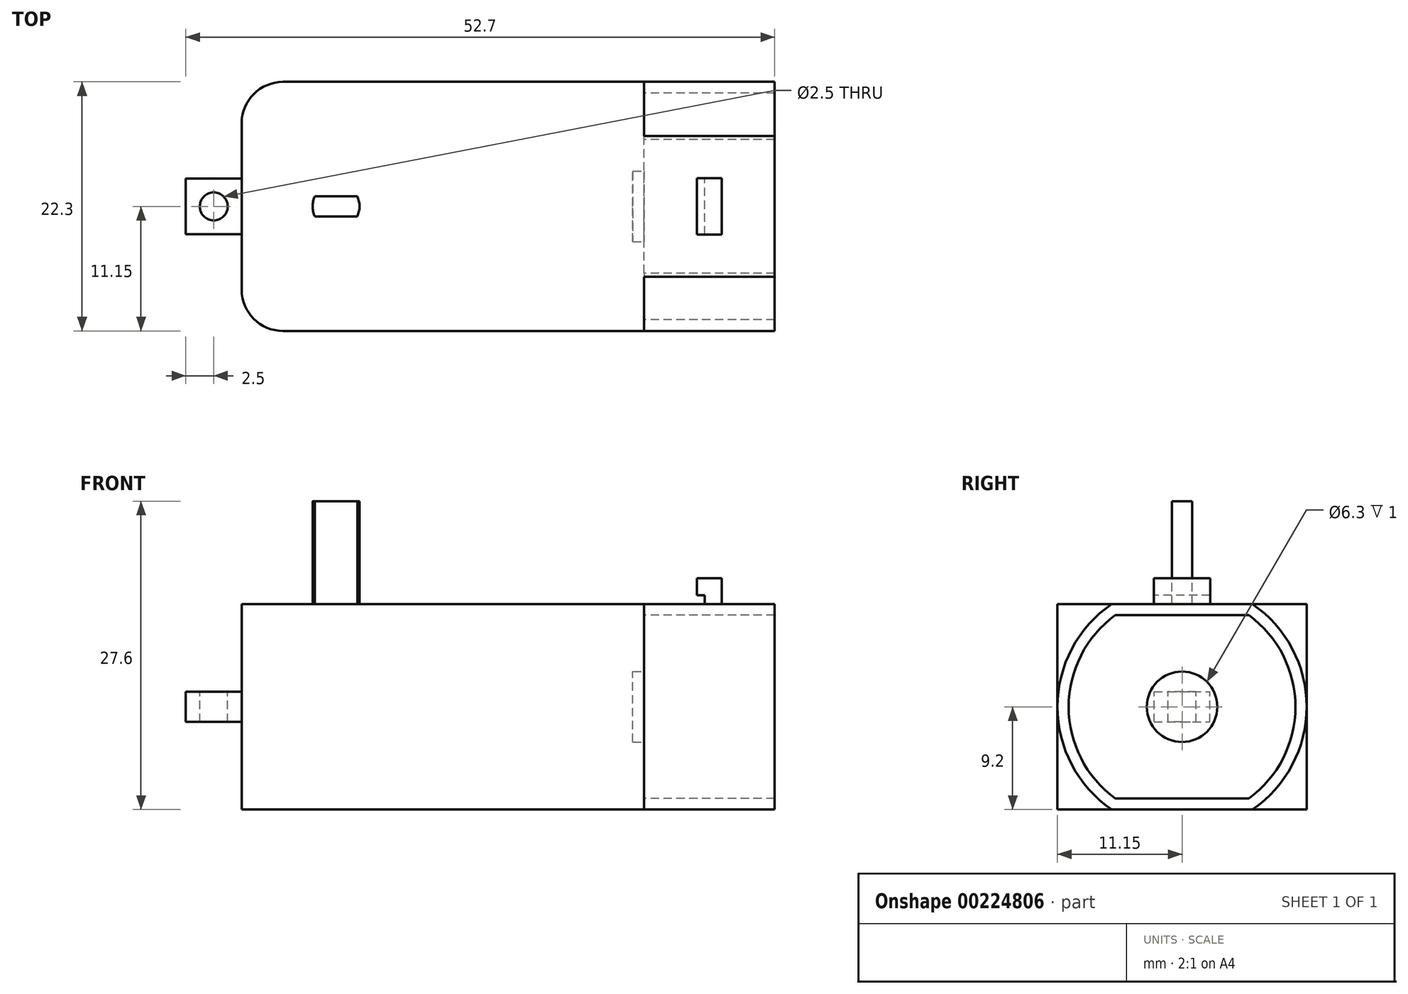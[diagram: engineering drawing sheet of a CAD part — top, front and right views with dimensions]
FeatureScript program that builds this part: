
annotation { "Feature Type Name" : "Feature", "Feature Type Description" : "" }
export const myFeature = defineFeature(function(context is Context, id is Id, definition is map)
    precondition{}
    {
        {
            var Q0;
            Q0=qCreatedBy(makeId("Top.planeOp"),FACE);
            var sketch = newSketch(context, id + "F0", { "sketchPlane" : qUnion([Q0])});
            skLineSegment(sketch, "E0.bottom", {"start": v(18, -11.15) * mm, "end": v(-18, -11.15) * mm});
            skLineSegment(sketch, "E0.top", {"start": v(18, 11.15) * mm, "end": v(-18, 11.15) * mm});
            skLineSegment(sketch, "E0.left", {"start": v(18, -11.15) * mm, "end": v(18, 11.15) * mm});
            skLineSegment(sketch, "E0.right", {"start": v(-18, -11.15) * mm, "end": v(-18, 11.15) * mm});
            skPoint(sketch, "E0.middle", {"position": v(0, 0) * mm});
            skSolve(sketch);
        }
        {
            var Q0;
            Q0 = qSketchRegion(id + "F0", true);
            extrude(context, id + "F1", {"entities" : qUnion([Q0]), "depth" : 18.4 * mm, "symmetric" : true});
        }
        {
            var Q0;
            Q0=makeQuery(id+"F1.opExtrude","SWEPT_FACE",FACE,{"disambiguationData":[OSD([sQuery(id+"F0.wireOp",EDGE,"E0.left")])]});
            var sketch = newSketch(context, id + "F2", { "sketchPlane" : qUnion([Q0])});
            skCircle(sketch, "E1", {"center": v(0, 0) * mm, "radius": 11.15 * mm});
            skCircle(sketch, "E2", {"center": v(0, 0) * mm, "radius": 3.15 * mm});
            skCircle(sketch, "E3", {"center": v(0, 0) * mm, "radius": 10.15 * mm});
            skLineSegment(sketch, "E4", {"start": v(-5.98, 8.2) * mm, "end": v(5.98, 8.2) * mm});
            skLineSegment(sketch, "E5", {"start": v(-5.98, -8.2) * mm, "end": v(5.98, -8.2) * mm});
            skSolve(sketch);
        }
        {
            var Q0;
            {var subQ0=sQuery(id+"F2.wireOp",EDGE,"E3");var subQ1=makeQuery(id+"F2.imprint","INTERSECT",VERTEX,{"disambiguationData":[OD(0.0)],"derivedFrom":[subQ0,sQuery(id+"F2.wireOp",EDGE,"E4")]});Q0=makeQuery(id+"F2.imprint","IMPRINT",FACE,{"disambiguationData":[TD([[makeQuery(id+"F2.imprint","IMPRINT",EDGE,{"disambiguationData":[TD([[subQ1,1.0]])],"derivedFrom":subQ0}),-1.0]])]});}
            var Q1;
            {var subQ0=sQuery(id+"F2.wireOp",EDGE,"E4");Q1=makeQuery(id+"F2.imprint","IMPRINT",FACE,{"disambiguationData":[TD([[makeQuery(id+"F2.imprint","IMPRINT",EDGE,{"derivedFrom":subQ0}),1.0]])]});}
            var Q2;
            {var subQ0=sQuery(id+"F2.wireOp",EDGE,"E3");var subQ5=makeQuery(id+"F2.imprint","INTERSECT",VERTEX,{"disambiguationData":[OD(1.0)],"derivedFrom":[subQ0,sQuery(id+"F2.wireOp",EDGE,"E4")]});Q2=makeQuery(id+"F2.imprint","IMPRINT",FACE,{"disambiguationData":[TD([[makeQuery(id+"F2.imprint","IMPRINT",EDGE,{"disambiguationData":[TD([[subQ5,-1.0]])],"derivedFrom":subQ0}),-1.0]])]});}
            var Q3;
            {var subQ0=sQuery(id+"F2.wireOp",EDGE,"E5");Q3=makeQuery(id+"F2.imprint","IMPRINT",FACE,{"disambiguationData":[TD([[makeQuery(id+"F2.imprint","IMPRINT",EDGE,{"derivedFrom":subQ0}),-1.0]])]});}
            extrude(context, id + "F3", {"entities" : qUnion([Q0, Q1, Q2, Q3]), "operationType" : NewBodyOperationType.ADD, "depth" : 11.7 * mm});
        }
        {
            var Q0;
            Q0=makeQuery(id+"F1.opExtrude","SWEPT_EDGE",EDGE,{"disambiguationData":[OSD([sQuery(id+"F0.wireOp",EDGE,"E0.bottom"),sQuery(id+"F0.wireOp",EDGE,"E0.right")])]});
            var Q1;
            Q1=makeQuery(id+"F1.opExtrude","SWEPT_EDGE",EDGE,{"disambiguationData":[OSD([sQuery(id+"F0.wireOp",EDGE,"E0.top"),sQuery(id+"F0.wireOp",EDGE,"E0.right")])]});
            fillet(context, id + "F4", {"entities" : qUnion([Q0, Q1]), "radius" : 3.7 * mm, "tangentPropagation" : true, "allowEdgeOverflow" : false});
        }
        {
            var Q0;
            Q0=makeQuery(id+"F2.imprint","IMPRINT",FACE,{"disambiguationData":[TD([[makeQuery(id+"F2.imprint","IMPRINT",EDGE,{"derivedFrom":sQuery(id+"F2.wireOp",EDGE,"E2")}),1.0]])]});
            extrude(context, id + "F5", {"entities" : qUnion([Q0]), "operationType" : NewBodyOperationType.REMOVE, "oppositeDirection" : true, "depth" : 1 * mm});
        }
        {
            var Q0;
            Q0=makeQuery(id+"F1.opExtrude","SWEPT_FACE",FACE,{"disambiguationData":[OSD([sQuery(id+"F0.wireOp",EDGE,"E0.right")])]});
            var sketch = newSketch(context, id + "F6", { "sketchPlane" : qUnion([Q0])});
            skLineSegment(sketch, "E6.bottom", {"start": v(2.5, -1.35) * mm, "end": v(-2.5, -1.35) * mm});
            skLineSegment(sketch, "E6.top", {"start": v(2.5, 1.35) * mm, "end": v(-2.5, 1.35) * mm});
            skLineSegment(sketch, "E6.left", {"start": v(2.5, -1.35) * mm, "end": v(2.5, 1.35) * mm});
            skLineSegment(sketch, "E6.right", {"start": v(-2.5, -1.35) * mm, "end": v(-2.5, 1.35) * mm});
            skPoint(sketch, "E6.middle", {"position": v(0, 0) * mm});
            skSolve(sketch);
        }
        {
            var Q0;
            Q0 = qSketchRegion(id + "F6", true);
            extrude(context, id + "F7", {"entities" : qUnion([Q0]), "operationType" : NewBodyOperationType.ADD, "depth" : 5 * mm});
        }
        {
            var Q0;
            {var subQ0=sQuery(id+"F2.wireOp",EDGE,"E3");var subQ1=sQuery(id+"F0.wireOp",EDGE,"E0.left");var subQ2=makeQuery(id+"F1.opExtrude","CAP_EDGE",EDGE,{"disambiguationData":[OSD([subQ1])],"isStart":false});var subQ3=makeQuery(id+"F2.imprint","INTERSECT",VERTEX,{"disambiguationData":[OD(0.0)],"derivedFrom":[subQ2,subQ0]});var subQ5=sQuery(id+"F2.wireOp",EDGE,"E1");Q0=makeQuery(id+"F3.boolean.opBoolean","MERGE",FACE,{"derivedFrom":[makeQuery(id+"F1.opExtrude","CAP_FACE",FACE,{"disambiguationData":[OSD([sQuery(id+"F0.wireOp",EDGE,"E0.bottom"),sQuery(id+"F0.wireOp",EDGE,"E0.top"),subQ1,sQuery(id+"F0.wireOp",EDGE,"E0.right")])],"isStart":false}),makeQuery(id+"F3.opExtrude","SWEPT_FACE",FACE,{"disambiguationData":[OSD([subQ1]),TDD([makeQuery(id+"F2.imprint","IMPRINT",EDGE,{"disambiguationData":[TD([[makeQuery(id+"F2.imprint","INTERSECT",VERTEX,{"disambiguationData":[OD(0.0)],"derivedFrom":[subQ2,subQ5]}),1.0]])],"derivedFrom":subQ2}),makeQuery(id+"F2.imprint","IMPRINT",EDGE,{"disambiguationData":[TD([[makeQuery(id+"F2.imprint","INTERSECT",VERTEX,{"disambiguationData":[OD(1.0)],"derivedFrom":[subQ2,subQ5]}),-1.0]])],"derivedFrom":subQ2}),makeQuery(id+"F2.imprint","IMPRINT",EDGE,{"disambiguationData":[TD([[subQ3,1.0]])],"derivedFrom":subQ2})])]})]});}
            var sketch = newSketch(context, id + "F8", { "sketchPlane" : qUnion([Q0])});
            skCircle(sketch, "E7", {"center": v(-15.89, 8.83) * mm, "radius": 0.9 * mm});
            skCircle(sketch, "E8", {"center": v(-3.22, 9.4) * mm, "radius": 0.5 * mm});
            skCircle(sketch, "E9", {"center": v(11.33, 8.81) * mm, "radius": 1.5 * mm});
            skCircle(sketch, "E10", {"center": v(15.04, 10.08) * mm, "radius": 0.5 * mm});
            skCircle(sketch, "E11", {"center": v(14.99, 7.05) * mm, "radius": 1.5 * mm});
            skCircle(sketch, "E12.MirrorC", {"center": v(-15.89, -8.83) * mm, "radius": 0.9 * mm});
            skCircle(sketch, "E13.MirrorC", {"center": v(-3.22, -9.4) * mm, "radius": 0.5 * mm});
            skCircle(sketch, "E14.MirrorC", {"center": v(11.33, -8.81) * mm, "radius": 1.5 * mm});
            skCircle(sketch, "E15.MirrorC", {"center": v(14.99, -7.05) * mm, "radius": 1.5 * mm});
            skCircle(sketch, "E16.MirrorC", {"center": v(15.04, -10.08) * mm, "radius": 0.5 * mm});
            skLineSegment(sketch, "E17.bottom", {"start": v(24.95, -2.52) * mm, "end": v(22.75, -2.52) * mm});
            skLineSegment(sketch, "E17.top", {"start": v(24.95, 2.52) * mm, "end": v(22.75, 2.52) * mm});
            skLineSegment(sketch, "E17.left", {"start": v(24.95, -2.52) * mm, "end": v(24.95, 2.52) * mm});
            skLineSegment(sketch, "E17.right", {"start": v(22.75, -2.52) * mm, "end": v(22.75, 2.52) * mm});
            skPoint(sketch, "E17.middle", {"position": v(23.85, 0) * mm});
            skPoint(sketch, "E17.middle.positionSnap0", {"position": v(29.7, 0) * mm});
            skPoint(sketch, "E17.middle.positionSnap1", {"position": v(23.85, 6.3) * mm});
            skPoint(sketch, "E17.centerSnap0", {"position": v(29.7, 0) * mm});
            skPoint(sketch, "E17.centerSnap1", {"position": v(23.85, 6.3) * mm});
            skLineSegment(sketch, "E18", {"start": v(-15.89, 8.83) * mm, "end": v(-3.22, 8.83) * mm, "construction": true});
            skCircle(sketch, "E19", {"center": v(-9.56, 0) * mm, "radius": 2.1 * mm});
            skPoint(sketch, "E19.centerSnap0", {"position": v(-9.56, 8.83) * mm});
            skSolve(sketch);
        }
        {
            var Q0;
            Q0=makeQuery(id+"F7.opExtrude","SWEPT_FACE",FACE,{"disambiguationData":[OSD([sQuery(id+"F6.wireOp",EDGE,"E6.top")])]});
            var sketch = newSketch(context, id + "F9", { "sketchPlane" : qUnion([Q0])});
            skCircle(sketch, "E20", {"center": v(-20.5, 0) * mm, "radius": 1.25 * mm});
            skPoint(sketch, "E20.centerSnap0", {"position": v(-23, 0) * mm});
            skPoint(sketch, "E20.centerSnap1", {"position": v(-20.5, 2.5) * mm});
            skSolve(sketch);
        }
        {
            var Q0;
            Q0 = qSketchRegion(id + "F9", true);
            extrude(context, id + "F10", {"entities" : qUnion([Q0]), "operationType" : NewBodyOperationType.REMOVE, "endBound" : BoundingType.THROUGH_ALL, "oppositeDirection" : true, "depth" : 25 * mm});
        }
        {
            var Q0;
            Q0=makeQuery(id+"F8.imprint","IMPRINT",FACE,{"disambiguationData":[TD([[makeQuery(id+"F8.imprint","IMPRINT",EDGE,{"derivedFrom":sQuery(id+"F8.wireOp",EDGE,"E17.bottom")}),-1.0]])]});
            extrude(context, id + "F11", {"entities" : qUnion([Q0]), "operationType" : NewBodyOperationType.ADD, "depth" : 2.3 * mm});
        }
        {
            var Q0;
            Q0=makeQuery(id+"F11.opExtrude","SWEPT_FACE",FACE,{"disambiguationData":[OSD([sQuery(id+"F8.wireOp",EDGE,"E17.right")])]});
            var sketch = newSketch(context, id + "F12", { "sketchPlane" : qUnion([Q0])});
            skLineSegment(sketch, "E21.bottom", {"start": v(-2.52, 9.2) * mm, "end": v(2.52, 9.2) * mm});
            skLineSegment(sketch, "E21.top", {"start": v(-2.52, 10) * mm, "end": v(2.52, 10) * mm});
            skLineSegment(sketch, "E21.left", {"start": v(-2.52, 9.2) * mm, "end": v(-2.52, 10) * mm});
            skLineSegment(sketch, "E21.right", {"start": v(2.52, 9.2) * mm, "end": v(2.52, 10) * mm});
            skSolve(sketch);
        }
        {
            var Q0;
            Q0 = qSketchRegion(id + "F12", true);
            extrude(context, id + "F13", {"entities" : qUnion([Q0]), "operationType" : NewBodyOperationType.REMOVE, "oppositeDirection" : true, "depth" : .7 * mm});
        }
        {
            var Q0;
            Q0=makeQuery(id+"F8.imprint","IMPRINT",FACE,{"disambiguationData":[TD([[makeQuery(id+"F8.imprint","IMPRINT",EDGE,{"derivedFrom":sQuery(id+"F8.wireOp",EDGE,"E19")}),1.0]])]});
            extrude(context, id + "F14", {"entities" : qUnion([Q0]), "operationType" : NewBodyOperationType.REMOVE, "endBound" : BoundingType.THROUGH_ALL, "oppositeDirection" : true, "depth" : 25 * mm});
        }
        {
            var Q0;
            Q0=makeQuery(id+"F8.imprint","IMPRINT",FACE,{"disambiguationData":[TD([[makeQuery(id+"F8.imprint","IMPRINT",EDGE,{"derivedFrom":sQuery(id+"F8.wireOp",EDGE,"E19")}),1.0]])]});
            var sketch = newSketch(context, id + "F15", { "sketchPlane" : qUnion([Q0])});
            skPoint(sketch, "E22.0", {"position": v(-9.56, 0) * mm});
            skCircle(sketch, "E22.1", {"center": v(-9.56, 0) * mm, "radius": 2.1 * mm});
            skSolve(sketch);
        }
        {
            var Q0;
            Q0 = qSketchRegion(id + "F15", true);
            extrude(context, id + "F16", {"entities" : qUnion([Q0]), "oppositeDirection" : true, "depth" : 18.4 * mm});
        }
        {
            var Q0;
            Q0=makeQuery(id+"F15.imprint","IMPRINT",FACE,{"disambiguationData":[TD([[makeQuery(id+"F15.imprint","IMPRINT",EDGE,{"derivedFrom":sQuery(id+"F15.wireOp",EDGE,"E22.1")}),1.0]])]});
            extrude(context, id + "F17", {"entities" : qUnion([Q0]), "operationType" : NewBodyOperationType.ADD, "depth" : 9.2 * mm});
        }
        {
            var Q0;
            Q0=makeQuery(id+"F17.opExtrude","CAP_FACE",FACE,{"disambiguationData":[OSD([sQuery(id+"F15.wireOp",EDGE,"E22.1")])],"isStart":false});
            var sketch = newSketch(context, id + "F18", { "sketchPlane" : qUnion([Q0])});
            skLineSegment(sketch, "E23", {"start": v(-11.46, 0.9) * mm, "end": v(-7.65, 0.9) * mm});
            skLineSegment(sketch, "E24.MirrorCS", {"start": v(-11.46, -0.9) * mm, "end": v(-7.65, -0.9) * mm});
            skSolve(sketch);
        }
        {
            var Q0;
            {var subQ0=sQuery(id+"F18.wireOp",EDGE,"E24.MirrorCS");Q0=makeQuery(id+"F18.imprint","IMPRINT",FACE,{"disambiguationData":[TD([[makeQuery(id+"F18.imprint","IMPRINT",EDGE,{"derivedFrom":subQ0}),-1.0]])]});}
            var Q1;
            {var subQ0=sQuery(id+"F18.wireOp",EDGE,"E23");Q1=makeQuery(id+"F18.imprint","IMPRINT",FACE,{"disambiguationData":[TD([[makeQuery(id+"F18.imprint","IMPRINT",EDGE,{"derivedFrom":subQ0}),1.0]])]});}
            extrude(context, id + "F19", {"entities" : qUnion([Q0, Q1]), "operationType" : NewBodyOperationType.REMOVE, "oppositeDirection" : true, "depth" : 9.2 * mm});
        }
    });
